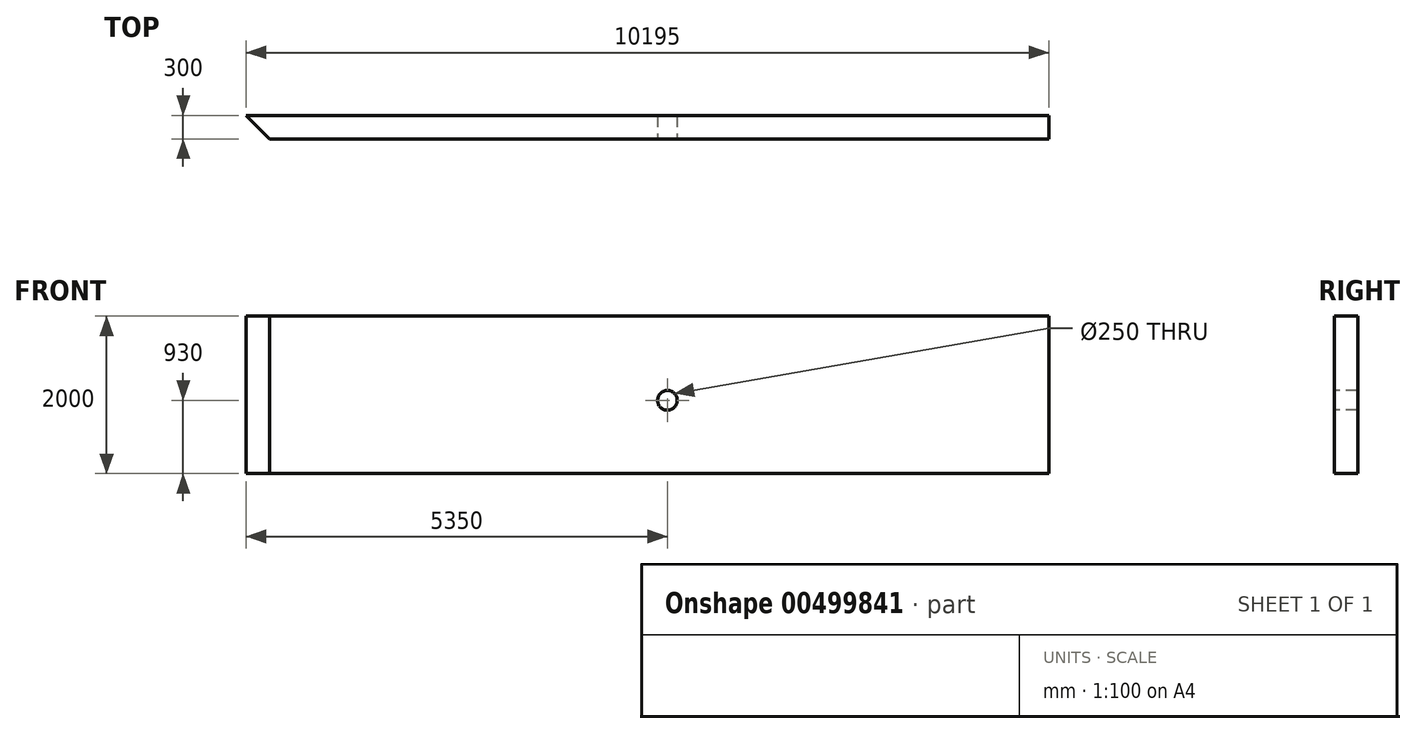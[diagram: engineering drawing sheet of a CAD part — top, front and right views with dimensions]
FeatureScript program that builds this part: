
annotation { "Feature Type Name" : "Feature", "Feature Type Description" : "" }
export const myFeature = defineFeature(function(context is Context, id is Id, definition is map)
    precondition{}
    {
        {
            var Q0;
            Q0=qCreatedBy(makeId("Top.planeOp"),FACE);
            var sketch = newSketch(context, id + "F0", { "sketchPlane" : qUnion([Q0])});
            skLineSegment(sketch, "E0", {"start": v(-9750, 0) * mm, "end": v(-9750, -2400) * mm});
            skLineSegment(sketch, "E1", {"start": v(-9750, -2400) * mm, "end": v(-9750, -2950) * mm});
            skLineSegment(sketch, "E2", {"start": v(-9750, -2950) * mm, "end": v(-9750, -6950) * mm});
            skLineSegment(sketch, "E3", {"start": v(-9750, -6950) * mm, "end": v(-2200, -6950) * mm});
            skLineSegment(sketch, "E4", {"start": v(-2200, -6950) * mm, "end": v(-2200, -2950) * mm});
            skLineSegment(sketch, "E5", {"start": v(-2200, -2950) * mm, "end": v(-7120, -2950) * mm});
            skLineSegment(sketch, "E6", {"start": v(-7120, -2950) * mm, "end": v(-7120, -2400) * mm});
            skLineSegment(sketch, "E7", {"start": v(-7120, -2400) * mm, "end": v(-6900, -2400) * mm});
            skLineSegment(sketch, "E8", {"start": v(-6900, -2400) * mm, "end": v(-6900, -2680) * mm});
            skLineSegment(sketch, "E9", {"start": v(-6900, -2680) * mm, "end": v(-1815, -2680) * mm});
            skLineSegment(sketch, "E10", {"start": v(-1815, -2680) * mm, "end": v(-1815, -2330) * mm});
            skLineSegment(sketch, "E11", {"start": v(-1815, -2330) * mm, "end": v(0, -2330) * mm});
            skLineSegment(sketch, "E12", {"start": v(0, -2330) * mm, "end": v(0, -1090) * mm});
            skLineSegment(sketch, "E13", {"start": v(0, -1090) * mm, "end": v(0, -240) * mm});
            skLineSegment(sketch, "E14", {"start": v(0, -240) * mm, "end": v(0, 0) * mm});
            skLineSegment(sketch, "E15", {"start": v(0, 0) * mm, "end": v(-9750, 0) * mm});
            skLineSegment(sketch, "E16", {"start": v(-9750, -2400) * mm, "end": v(-8150, -2400) * mm});
            skLineSegment(sketch, "E17", {"start": v(-8150, -2400) * mm, "end": v(-8150, -2950) * mm});
            skLineSegment(sketch, "E18", {"start": v(-8150, -2950) * mm, "end": v(-9750, -2950) * mm});
            skLineSegment(sketch, "E19", {"start": v(-6420, -2950) * mm, "end": v(-6420, -4010) * mm});
            skLineSegment(sketch, "E20", {"start": v(-6420, -4010) * mm, "end": v(-5360, -4010) * mm});
            skLineSegment(sketch, "E21", {"start": v(-5360, -4010) * mm, "end": v(-5360, -2950) * mm});
            skLineSegment(sketch, "E22", {"start": v(0, 0) * mm, "end": v(145, 0) * mm});
            skLineSegment(sketch, "E23", {"start": v(145, 0) * mm, "end": v(145, -5370) * mm});
            skLineSegment(sketch, "E24", {"start": v(145, -5370) * mm, "end": v(0, -5370) * mm});
            skLineSegment(sketch, "E25", {"start": v(0, -5370) * mm, "end": v(0, -2330) * mm});
            skLineSegment(sketch, "E26", {"start": v(0, -2475) * mm, "end": v(-1670, -2475) * mm});
            skLineSegment(sketch, "E27", {"start": v(-1670, -2475) * mm, "end": v(-1670, -2950) * mm});
            skLineSegment(sketch, "E28", {"start": v(-1670, -2950) * mm, "end": v(-1900, -2950) * mm});
            skLineSegment(sketch, "E29", {"start": v(-1900, -2950) * mm, "end": v(-1900, -7250) * mm});
            skLineSegment(sketch, "E30", {"start": v(-1900, -7250) * mm, "end": v(-2200, -6950) * mm});
            skLineSegment(sketch, "E31", {"start": v(-1900, -7250) * mm, "end": v(-10050, -7250) * mm});
            skLineSegment(sketch, "E32", {"start": v(-10050, -7250) * mm, "end": v(-9750, -6950) * mm});
            skLineSegment(sketch, "E33", {"start": v(-10050, -7250) * mm, "end": v(-10050, 300) * mm});
            skLineSegment(sketch, "E34", {"start": v(-10050, 300) * mm, "end": v(-9750, 0) * mm});
            skLineSegment(sketch, "E35", {"start": v(-10050, 300) * mm, "end": v(145, 300) * mm});
            skLineSegment(sketch, "E36", {"start": v(145, 300) * mm, "end": v(145, 0) * mm});
            skLineSegment(sketch, "E37", {"start": v(-8150, -2400) * mm, "end": v(-7120, -2400) * mm});
            skSolve(sketch);
        }
        {
            var Q0;
            Q0=makeQuery(id+"F0.imprint","IMPRINT",FACE,{"disambiguationData":[TD([[makeQuery(id+"F0.imprint","IMPRINT",EDGE,{"derivedFrom":sQuery(id+"F0.wireOp",EDGE,"E15")}),-1.0]])]});
            extrude(context, id + "F1", {"entities" : qUnion([Q0]), "depth" : 2000 * mm});
        }
        {
            var Q0;
            Q0=qCreatedBy(makeId("Front.planeOp"),FACE);
            var sketch = newSketch(context, id + "F2", { "sketchPlane" : qUnion([Q0])});
            skLineSegment(sketch, "E38", {"start": v(-1810, 0) * mm, "end": v(-1810, 210) * mm});
            skLineSegment(sketch, "E39", {"start": v(-1810, 210) * mm, "end": v(-2080, 210) * mm});
            skLineSegment(sketch, "E40", {"start": v(-2080, 210) * mm, "end": v(-2080, 380) * mm});
            skLineSegment(sketch, "E41", {"start": v(-2080, 380) * mm, "end": v(-7320, 380) * mm});
            skLineSegment(sketch, "E42", {"start": v(-7320, 380) * mm, "end": v(-7320, 1080) * mm});
            skLineSegment(sketch, "E43", {"start": v(-7320, 1080) * mm, "end": v(-9750, 1080) * mm});
            skLineSegment(sketch, "E44", {"start": v(-9750, 1080) * mm, "end": v(-9750, 0) * mm});
            skLineSegment(sketch, "E45", {"start": v(-9750, 0) * mm, "end": v(-1810, 0) * mm});
            skCircle(sketch, "E46", {"center": v(-4700, 930) * mm, "radius": 125 * mm});
            skSolve(sketch);
        }
        {
            var Q0;
            Q0=makeQuery(id+"F2.imprint","IMPRINT",FACE,{"disambiguationData":[TD([[makeQuery(id+"F2.imprint","IMPRINT",EDGE,{"derivedFrom":sQuery(id+"F2.wireOp",EDGE,"E46")}),1.0]])]});
            extrude(context, id + "F3", {"entities" : qUnion([Q0]), "operationType" : NewBodyOperationType.REMOVE, "endBound" : BoundingType.THROUGH_ALL, "oppositeDirection" : true, "depth" : 25 * mm});
        }
    });
